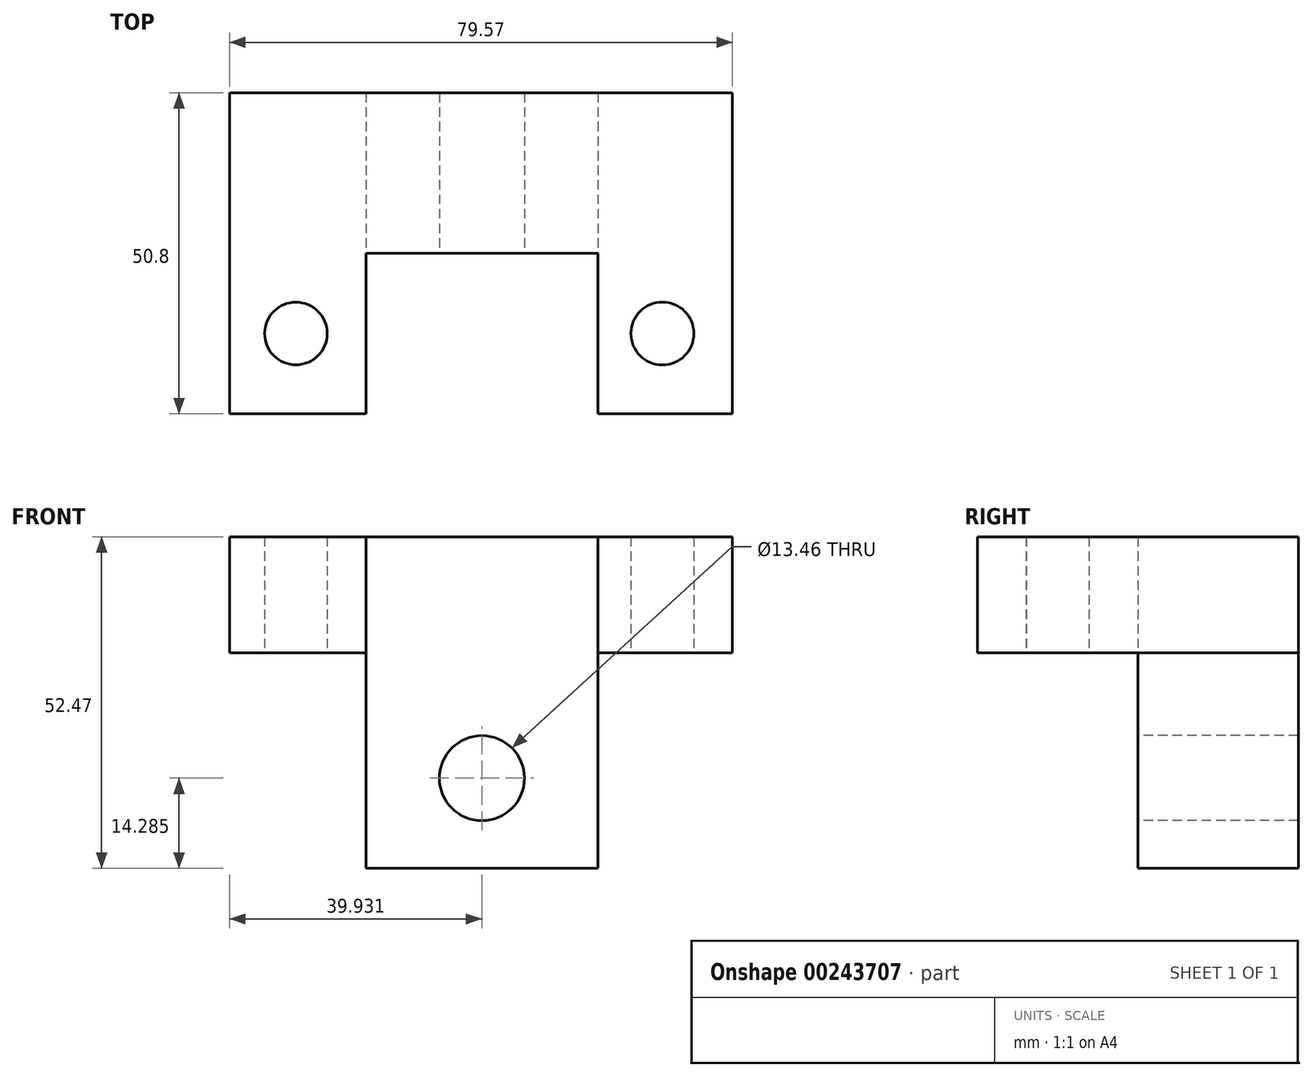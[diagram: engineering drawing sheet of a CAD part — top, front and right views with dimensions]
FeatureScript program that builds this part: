
annotation { "Feature Type Name" : "Feature", "Feature Type Description" : "" }
export const myFeature = defineFeature(function(context is Context, id is Id, definition is map)
    precondition{}
    {
        {
            var Q0;
            Q0=qCreatedBy(makeId("Front.planeOp"),FACE);
            var sketch = newSketch(context, id + "F0", { "sketchPlane" : qUnion([Q0])});
            skLineSegment(sketch, "E0.bottom", {"start": v(-27.98, 24.34) * mm, "end": v(51.6, 24.34) * mm});
            skLineSegment(sketch, "E0.top", {"start": v(-27.98, -28.13) * mm, "end": v(51.6, -28.13) * mm});
            skLineSegment(sketch, "E0.left", {"start": v(-27.98, 24.34) * mm, "end": v(-27.98, -28.13) * mm});
            skLineSegment(sketch, "E0.right", {"start": v(51.6, 24.34) * mm, "end": v(51.6, -28.13) * mm});
            skSolve(sketch);
        }
        {
            var Q0;
            Q0 = qSketchRegion(id + "F0", true);
            extrude(context, id + "F1", {"entities" : qUnion([Q0]), "depth" : 25.4 * mm});
        }
        {
            var Q0;
            Q0=makeQuery(id+"F1.opExtrude","CAP_FACE",FACE,{"disambiguationData":[OSD([sQuery(id+"F0.wireOp",EDGE,"E0.bottom"),sQuery(id+"F0.wireOp",EDGE,"E0.top"),sQuery(id+"F0.wireOp",EDGE,"E0.left"),sQuery(id+"F0.wireOp",EDGE,"E0.right")])],"isStart":false});
            var sketch = newSketch(context, id + "F2", { "sketchPlane" : qUnion([Q0])});
            skLineSegment(sketch, "E1", {"start": v(-6.41, 24.34) * mm, "end": v(-6.41, 5.98) * mm});
            skLineSegment(sketch, "E2", {"start": v(-6.41, 5.98) * mm, "end": v(-27.98, 5.98) * mm});
            skLineSegment(sketch, "E3", {"start": v(30.31, 24.34) * mm, "end": v(30.31, 5.98) * mm});
            skLineSegment(sketch, "E4", {"start": v(30.31, 5.98) * mm, "end": v(51.6, 5.98) * mm});
            skSolve(sketch);
        }
        {
            var Q0;
            {var subQ0=sQuery(id+"F2.wireOp",EDGE,"E1");Q0=makeQuery(id+"F2.imprint","IMPRINT",FACE,{"disambiguationData":[TD([[makeQuery(id+"F2.imprint","IMPRINT",EDGE,{"derivedFrom":subQ0}),-1.0]])]});}
            var Q1;
            {var subQ0=sQuery(id+"F2.wireOp",EDGE,"E3");Q1=makeQuery(id+"F2.imprint","IMPRINT",FACE,{"disambiguationData":[TD([[makeQuery(id+"F2.imprint","IMPRINT",EDGE,{"derivedFrom":subQ0}),1.0]])]});}
            extrude(context, id + "F3", {"entities" : qUnion([Q0, Q1]), "operationType" : NewBodyOperationType.ADD, "depth" : 25.4 * mm});
        }
        {
            var Q0;
            Q0=makeQuery(id+"F1.opExtrude","CAP_FACE",FACE,{"disambiguationData":[OSD([sQuery(id+"F0.wireOp",EDGE,"E0.bottom"),sQuery(id+"F0.wireOp",EDGE,"E0.top"),sQuery(id+"F0.wireOp",EDGE,"E0.left"),sQuery(id+"F0.wireOp",EDGE,"E0.right")])],"isStart":false});
            var sketch = newSketch(context, id + "F4", { "sketchPlane" : qUnion([Q0])});
            skLineSegment(sketch, "E5", {"start": v(-6.41, 5.98) * mm, "end": v(-6.41, -28.13) * mm});
            skLineSegment(sketch, "E6", {"start": v(30.31, 5.98) * mm, "end": v(30.31, -28.13) * mm});
            skSolve(sketch);
        }
        {
            var Q0;
            {var subQ0=sQuery(id+"F4.wireOp",EDGE,"E5");Q0=makeQuery(id+"F4.imprint","IMPRINT",FACE,{"disambiguationData":[TD([[makeQuery(id+"F4.imprint","IMPRINT",EDGE,{"derivedFrom":subQ0}),-1.0]])]});}
            var Q1;
            {var subQ0=sQuery(id+"F4.wireOp",EDGE,"E6");Q1=makeQuery(id+"F4.imprint","IMPRINT",FACE,{"disambiguationData":[TD([[makeQuery(id+"F4.imprint","IMPRINT",EDGE,{"derivedFrom":subQ0}),1.0]])]});}
            extrude(context, id + "F5", {"entities" : qUnion([Q0, Q1]), "operationType" : NewBodyOperationType.REMOVE, "oppositeDirection" : true, "depth" : 25.4 * mm});
        }
        {
            var Q0;
            Q0=makeQuery(id+"F1.opExtrude","CAP_FACE",FACE,{"disambiguationData":[OSD([sQuery(id+"F0.wireOp",EDGE,"E0.bottom"),sQuery(id+"F0.wireOp",EDGE,"E0.top"),sQuery(id+"F0.wireOp",EDGE,"E0.left"),sQuery(id+"F0.wireOp",EDGE,"E0.right")])],"isStart":false});
            var sketch = newSketch(context, id + "F6", { "sketchPlane" : qUnion([Q0])});
            skCircle(sketch, "E7", {"center": v(11.95, -13.85) * mm, "radius": 6.73 * mm});
            skPoint(sketch, "E7.centerSnap0", {"position": v(11.95, -28.13) * mm});
            skSolve(sketch);
        }
        {
            var Q0;
            Q0 = qSketchRegion(id + "F6", true);
            extrude(context, id + "F7", {"entities" : qUnion([Q0]), "operationType" : NewBodyOperationType.REMOVE, "oppositeDirection" : true, "depth" : 25.4 * mm});
        }
        {
            var Q0;
            {var subQ0=sQuery(id+"F2.wireOp",EDGE,"E2");Q0=makeQuery(id+"F5.boolean.opBoolean","MERGE",FACE,{"derivedFrom":[makeQuery(id+"F3.opExtrude","SWEPT_FACE",FACE,{"disambiguationData":[OSD([subQ0])]}),makeQuery(id+"F5.opExtrude","SWEPT_FACE",FACE,{"disambiguationData":[OSD([subQ0])]})]});}
            var sketch = newSketch(context, id + "F8", { "sketchPlane" : qUnion([Q0])});
            skCircle(sketch, "E8", {"center": v(-17.49, 38.1) * mm, "radius": 4.96 * mm});
            skPoint(sketch, "E8.centerSnap0", {"position": v(-6.41, 38.1) * mm});
            skSolve(sketch);
        }
        {
            var Q0;
            Q0 = qSketchRegion(id + "F8", true);
            extrude(context, id + "F9", {"entities" : qUnion([Q0]), "operationType" : NewBodyOperationType.REMOVE, "oppositeDirection" : true, "depth" : 25.4 * mm});
        }
        {
            var Q0;
            {var subQ0=sQuery(id+"F2.wireOp",EDGE,"E4");Q0=makeQuery(id+"F5.boolean.opBoolean","MERGE",FACE,{"derivedFrom":[makeQuery(id+"F3.opExtrude","SWEPT_FACE",FACE,{"disambiguationData":[OSD([subQ0])]}),makeQuery(id+"F5.opExtrude","SWEPT_FACE",FACE,{"disambiguationData":[OSD([subQ0])]})]});}
            var sketch = newSketch(context, id + "F10", { "sketchPlane" : qUnion([Q0])});
            skCircle(sketch, "E9", {"center": v(40.52, 38.1) * mm, "radius": 4.98 * mm});
            skPoint(sketch, "E9.centerSnap0", {"position": v(30.31, 38.1) * mm});
            skSolve(sketch);
        }
        {
            var Q0;
            Q0 = qSketchRegion(id + "F10", true);
            extrude(context, id + "F11", {"entities" : qUnion([Q0]), "operationType" : NewBodyOperationType.REMOVE, "oppositeDirection" : true, "depth" : 25.4 * mm});
        }
    });
